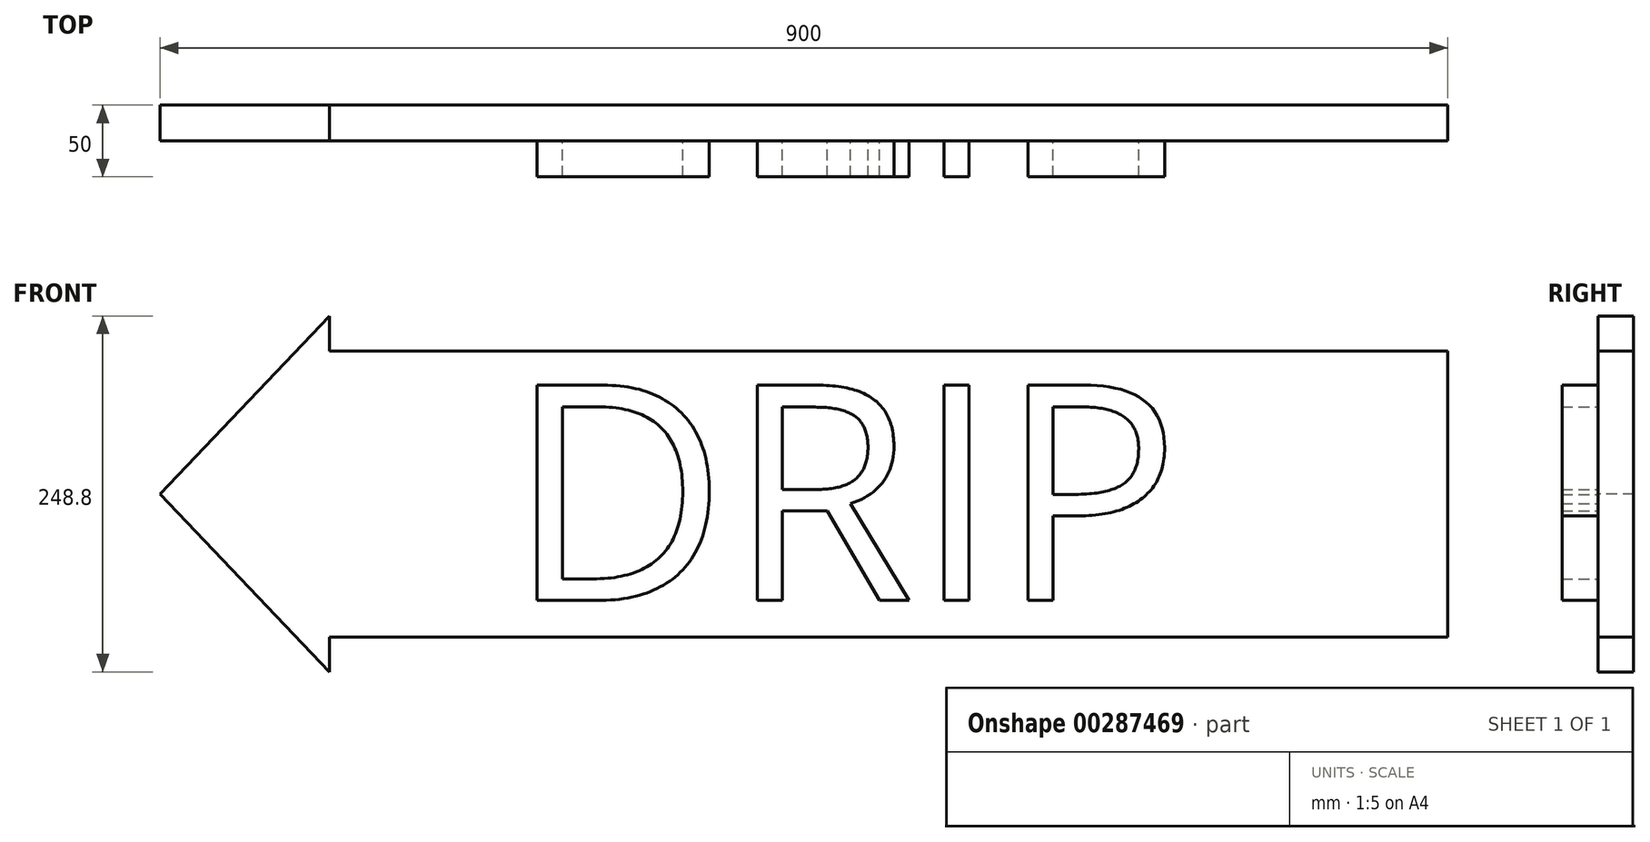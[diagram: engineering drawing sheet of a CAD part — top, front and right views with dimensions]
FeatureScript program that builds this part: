
annotation { "Feature Type Name" : "Feature", "Feature Type Description" : "" }
export const myFeature = defineFeature(function(context is Context, id is Id, definition is map)
    precondition{}
    {
        {
            var Q0;
            Q0=qCreatedBy(makeId("Front.planeOp"),FACE);
            var sketch = newSketch(context, id + "F0", { "sketchPlane" : qUnion([Q0])});
            skLineSegment(sketch, "E0", {"start": v(0, 0) * mm, "end": v(0, 100) * mm});
            skLineSegment(sketch, "E1.MirrorCS", {"start": v(0, 0) * mm, "end": v(0, -100) * mm});
            skLineSegment(sketch, "E2.MirrorCS", {"start": v(-781.62, 100) * mm, "end": v(-781.62, 124.4) * mm});
            skLineSegment(sketch, "E3.MirrorCS", {"start": v(-781.62, -100) * mm, "end": v(-781.62, -124.4) * mm});
            skLineSegment(sketch, "E4.MirrorCS", {"start": v(-781.62, 124.4) * mm, "end": v(-900, 0) * mm});
            skLineSegment(sketch, "E5.MirrorCS", {"start": v(0, 100) * mm, "end": v(-781.62, 100) * mm});
            skLineSegment(sketch, "E6.MirrorCS", {"start": v(0, -100) * mm, "end": v(-781.62, -100) * mm});
            skLineSegment(sketch, "E7.MirrorCS", {"start": v(-781.62, -124.4) * mm, "end": v(-900, 0) * mm});
            skLineSegment(sketch, "E8.MirrorCS", {"start": v(-900, 0) * mm, "end": v(0, 0) * mm});
            skSolve(sketch);
        }
        {
            var Q0;
            Q0=qSketchRegion(id+"F0",true);
            extrude(context, id + "F1", {"entities" : qUnion([Q0]), "oppositeDirection" : true, "depth" : 25 * mm});
        }
        {
            var Q0;
            Q0=qCreatedBy(makeId("Front.planeOp"),FACE);
            var sketch = newSketch(context, id + "F2", { "sketchPlane" : qUnion([Q0])});
            skText(sketch, "E9", { "text": "DRIP", "fontName": "OpenSans-Regular.ttf"});
            const initialGuessF2  = {"E9": [-0.6571, -0.07451, 1, 0, 0.15191]};
            skSetInitialGuess(sketch, initialGuessF2);
            skSolve(sketch);
        }
        {
            var Q0;
            Q0=qSketchRegion(id+"F2",true);
            extrude(context, id + "F3", {"entities" : qUnion([Q0]), "operationType" : NewBodyOperationType.ADD, "depth" : 25 * mm});
        }
    });
